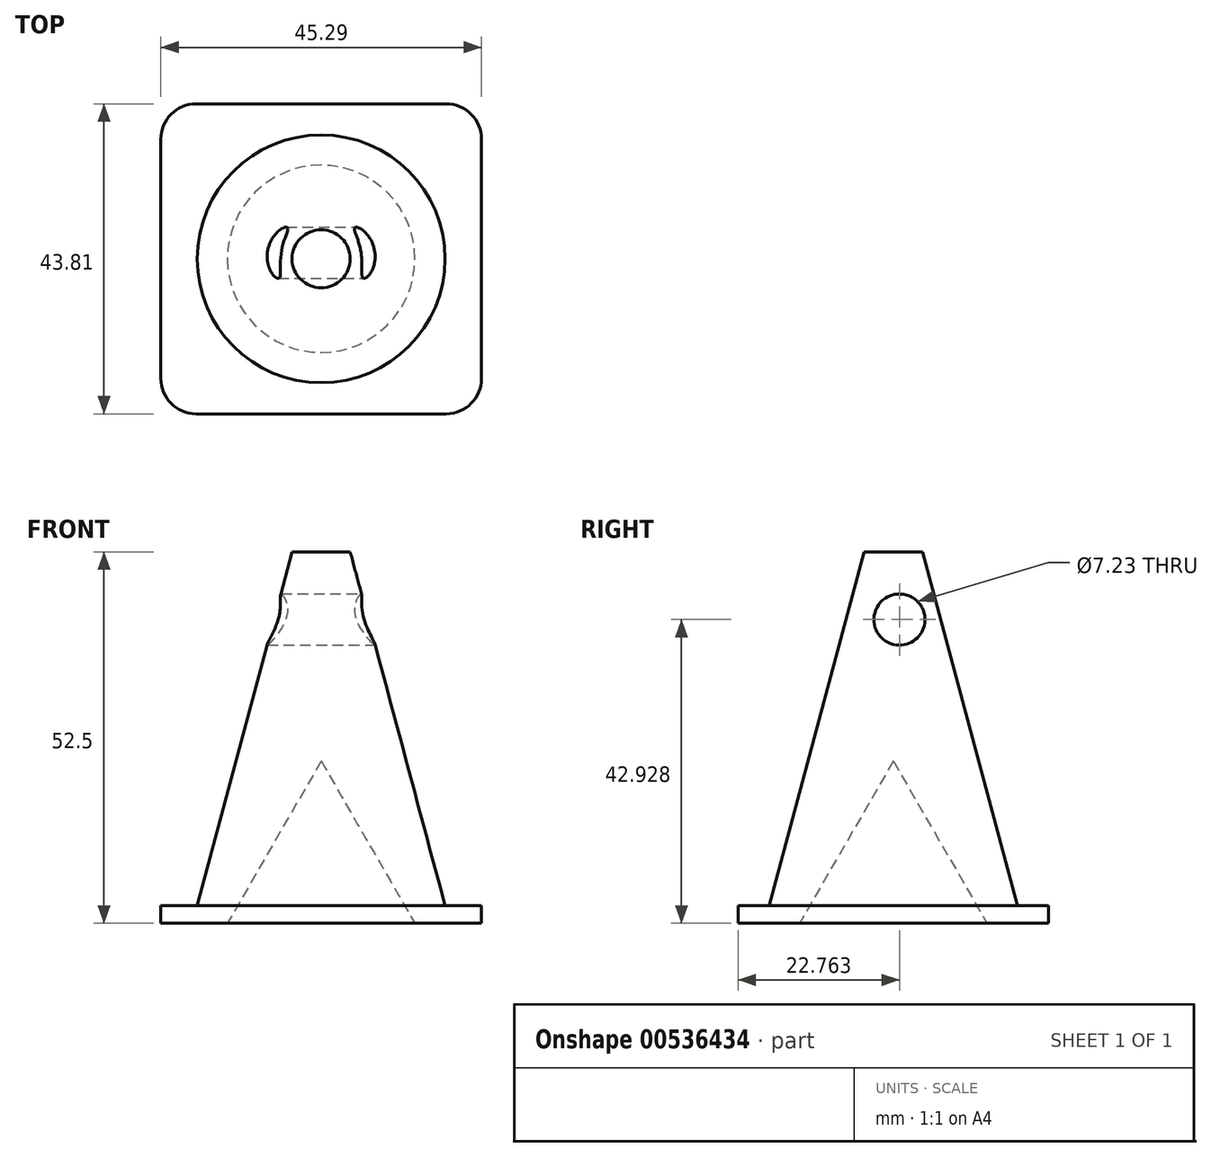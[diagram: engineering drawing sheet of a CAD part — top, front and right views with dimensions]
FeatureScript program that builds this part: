
annotation { "Feature Type Name" : "Feature", "Feature Type Description" : "" }
export const myFeature = defineFeature(function(context is Context, id is Id, definition is map)
    precondition{}
    {
        {
            var Q0;
            Q0=qCreatedBy(makeId("Top.planeOp"),FACE);
            var sketch = newSketch(context, id + "F0", { "sketchPlane" : qUnion([Q0])});
            skArc(sketch, "E0", {"start": v(-35.3, 38.8) * mm, "mid": v(-38.83, 37.34) * mm, "end": v(-40.3, 33.8) * mm});
            skArc(sketch, "E1", {"start": v(-40.3, 0) * mm, "mid": v(-38.83, -3.54) * mm, "end": v(-35.3, -5) * mm});
            skArc(sketch, "E2", {"start": v(0, -5) * mm, "mid": v(3.54, -3.54) * mm, "end": v(5, 0) * mm});
            skArc(sketch, "E3", {"start": v(5, 33.8) * mm, "mid": v(3.54, 37.34) * mm, "end": v(0, 38.8) * mm});
            skLineSegment(sketch, "E4", {"start": v(-40.3, 33.8) * mm, "end": v(-40.3, 0) * mm});
            skLineSegment(sketch, "E5", {"start": v(-35.3, -5) * mm, "end": v(0, -5) * mm});
            skLineSegment(sketch, "E6", {"start": v(5, 0) * mm, "end": v(5, 33.8) * mm});
            skLineSegment(sketch, "E7", {"start": v(-35.3, 38.8) * mm, "end": v(0, 38.8) * mm});
            skCircle(sketch, "E8", {"center": v(-17.65, 16.9) * mm, "radius": 17.5 * mm});
            skSolve(sketch);
        }
        {
            var Q0;
            Q0=makeQuery(id+"F0.imprint","IMPRINT",FACE,{"disambiguationData":[TD([[makeQuery(id+"F0.imprint","IMPRINT",EDGE,{"derivedFrom":sQuery(id+"F0.wireOp",EDGE,"E0")}),1.0]])]});
            var Q1;
            Q1=makeQuery(id+"F0.imprint","IMPRINT",FACE,{"disambiguationData":[TD([[makeQuery(id+"F0.imprint","IMPRINT",EDGE,{"derivedFrom":sQuery(id+"F0.wireOp",EDGE,"E8")}),1.0]])]});
            extrude(context, id + "F1", {"entities" : qUnion([Q0, Q1]), "depth" : 2.5 * mm, "offsetDistance" : 25 * mm});
        }
        {
            var Q0;
            Q0=makeQuery(id+"F1.opExtrude","CAP_FACE",FACE,{"disambiguationData":[OSD([sQuery(id+"F0.wireOp",EDGE,"E0"),sQuery(id+"F0.wireOp",EDGE,"E1"),sQuery(id+"F0.wireOp",EDGE,"E2"),sQuery(id+"F0.wireOp",EDGE,"E3"),sQuery(id+"F0.wireOp",EDGE,"E4"),sQuery(id+"F0.wireOp",EDGE,"E5"),sQuery(id+"F0.wireOp",EDGE,"E6"),sQuery(id+"F0.wireOp",EDGE,"E7")])],"isStart":false});
            var sketch = newSketch(context, id + "F2", { "sketchPlane" : qUnion([Q0])});
            skCircle(sketch, "E9", {"center": v(-17.65, 16.9) * mm, "radius": 17.5 * mm});
            skPoint(sketch, "E10.orphan", {"position": v(-40.3, 16.9) * mm});
            skPoint(sketch, "E11.orphan", {"position": v(-17.65, -5) * mm});
            skPoint(sketch, "E12.start.orphan", {"position": v(5, 16.9) * mm});
            skPoint(sketch, "E13.start.orphan", {"position": v(-17.65, 38.8) * mm});
            skSolve(sketch);
        }
        {
            var Q0;
            Q0=makeQuery(id+"F2.imprint","IMPRINT",FACE,{"disambiguationData":[TD([[makeQuery(id+"F2.imprint","IMPRINT",EDGE,{"derivedFrom":sQuery(id+"F2.wireOp",EDGE,"E9")}),1.0]])]});
            extrude(context, id + "F3", {"entities" : qUnion([Q0]), "operationType" : NewBodyOperationType.ADD, "depth" : 50 * mm, "offsetDistance" : 25 * mm, "hasDraft" : true, "draftAngle" : 15 * degree, "draftPullDirection" : true});
        }
        {
            var Q0;
            Q0=qCreatedBy(makeId("Right.planeOp"),FACE);
            var sketch = newSketch(context, id + "F4", { "sketchPlane" : qUnion([Q0])});
            skCircle(sketch, "E14", {"center": v(17.76, 42.93) * mm, "radius": 3.61 * mm});
            skSolve(sketch);
        }
        {
            var Q0;
            Q0 = qSketchRegion(id + "F4", true);
            extrude(context, id + "F5", {"entities" : qUnion([Q0]), "operationType" : NewBodyOperationType.REMOVE, "oppositeDirection" : true, "depth" : 60 * mm, "offsetDistance" : 25 * mm});
        }
        {
            var Q0;
            Q0=makeQuery(id+"F1.opExtrude","CAP_FACE",FACE,{"disambiguationData":[OSD([sQuery(id+"F0.wireOp",EDGE,"E0"),sQuery(id+"F0.wireOp",EDGE,"E1"),sQuery(id+"F0.wireOp",EDGE,"E2"),sQuery(id+"F0.wireOp",EDGE,"E3"),sQuery(id+"F0.wireOp",EDGE,"E4"),sQuery(id+"F0.wireOp",EDGE,"E5"),sQuery(id+"F0.wireOp",EDGE,"E6"),sQuery(id+"F0.wireOp",EDGE,"E7")])],"isStart":true});
            var sketch = newSketch(context, id + "F6", { "sketchPlane" : qUnion([Q0])});
            skCircle(sketch, "E15", {"center": v(-17.65, -16.9) * mm, "radius": 13.23 * mm});
            skSolve(sketch);
        }
        {
            var Q0;
            Q0=makeQuery(id+"F6.imprint","IMPRINT",FACE,{"disambiguationData":[TD([[makeQuery(id+"F6.imprint","IMPRINT",EDGE,{"derivedFrom":sQuery(id+"F6.wireOp",EDGE,"E15")}),1.0]])]});
            extrude(context, id + "F7", {"entities" : qUnion([Q0]), "operationType" : NewBodyOperationType.REMOVE, "oppositeDirection" : true, "depth" : 54.2 * mm, "offsetDistance" : 25 * mm, "hasDraft" : true, "draftAngle" : 30 * degree, "draftPullDirection" : true});
        }
    });
